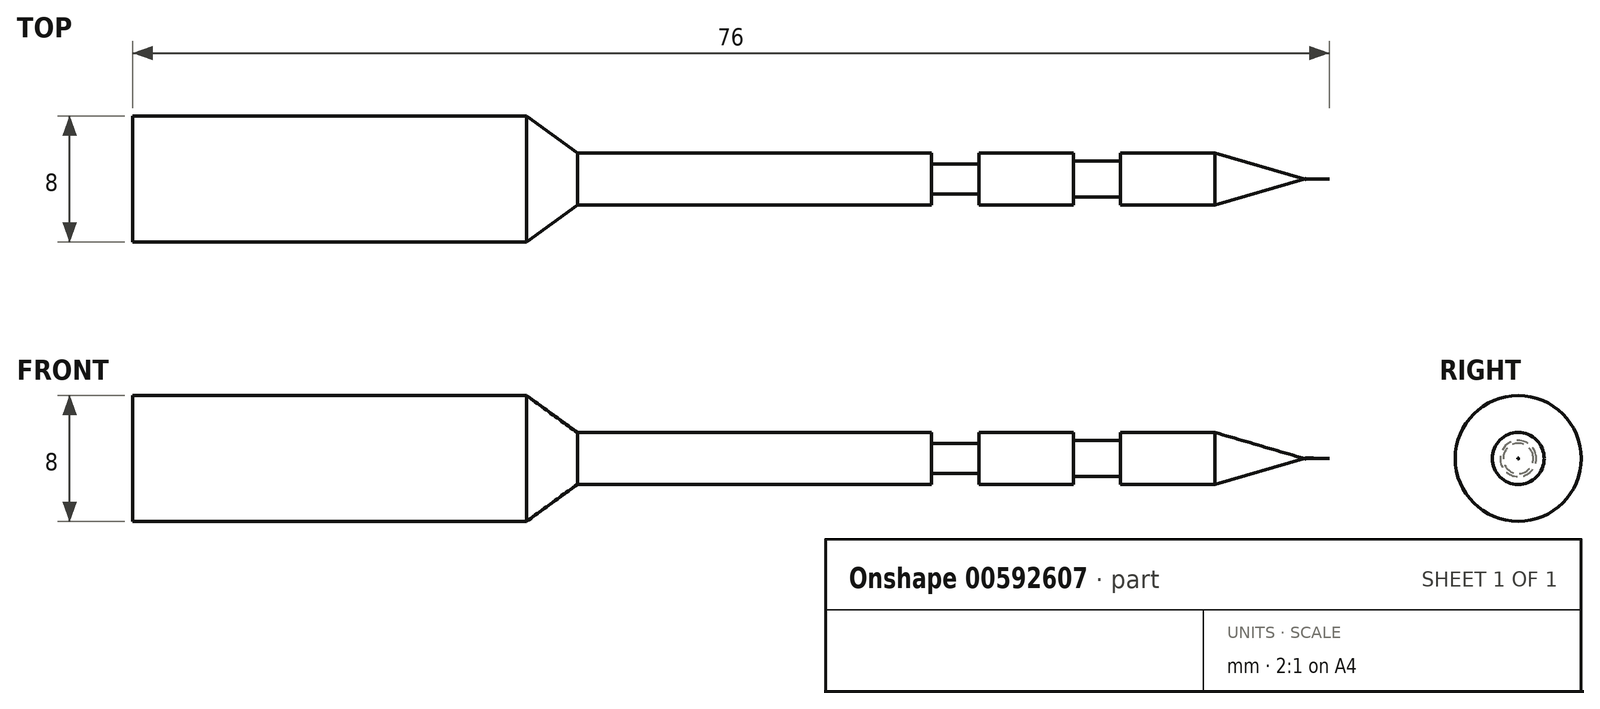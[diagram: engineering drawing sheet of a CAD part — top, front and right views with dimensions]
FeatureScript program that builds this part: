
annotation { "Feature Type Name" : "Feature", "Feature Type Description" : "" }
export const myFeature = defineFeature(function(context is Context, id is Id, definition is map)
    precondition{}
    {
        {
            var Q0;
            Q0=qCreatedBy(makeId("Front.planeOp"),FACE);
            var sketch = newSketch(context, id + "F0", { "sketchPlane" : qUnion([Q0])});
            skLineSegment(sketch, "E0", {"start": v(-71.02, 0) * mm, "end": v(-71.02, 4) * mm});
            skLineSegment(sketch, "E1", {"start": v(-71.02, 4) * mm, "end": v(-46.02, 4) * mm});
            skLineSegment(sketch, "E2", {"start": v(-46.02, 4) * mm, "end": v(-42.78, 1.65) * mm});
            skLineSegment(sketch, "E3", {"start": v(-42.78, 1.65) * mm, "end": v(-20.28, 1.65) * mm});
            skLineSegment(sketch, "E4", {"start": v(-20.28, 1.65) * mm, "end": v(-20.28, 0.96) * mm});
            skLineSegment(sketch, "E5", {"start": v(-20.28, 0.96) * mm, "end": v(-17.28, 0.96) * mm});
            skLineSegment(sketch, "E6", {"start": v(-17.28, 0.96) * mm, "end": v(-17.28, 1.65) * mm});
            skLineSegment(sketch, "E7", {"start": v(-17.28, 1.65) * mm, "end": v(-11.28, 1.65) * mm});
            skLineSegment(sketch, "E8", {"start": v(-11.28, 1.65) * mm, "end": v(-11.28, 1.15) * mm});
            skLineSegment(sketch, "E9", {"start": v(-11.28, 1.15) * mm, "end": v(-8.28, 1.15) * mm});
            skLineSegment(sketch, "E10", {"start": v(-8.28, 1.15) * mm, "end": v(-8.28, 1.65) * mm});
            skLineSegment(sketch, "E11", {"start": v(-8.28, 1.65) * mm, "end": v(-2.28, 1.65) * mm});
            skLineSegment(sketch, "E12", {"start": v(-2.28, 1.65) * mm, "end": v(3.48, -0.03) * mm});
            skLineSegment(sketch, "E13", {"start": v(3.48, -0.03) * mm, "end": v(4.98, 0) * mm});
            skLineSegment(sketch, "E14", {"start": v(4.98, 0) * mm, "end": v(-71.02, 0) * mm});
            skSolve(sketch);
        }
        {
            var Q0;
            Q0 = qSketchRegion(id + "F0", true);
            var Q1;
            Q1=sQuery(id+"F0.wireOp",EDGE,"E14");
            revolve(context, id + "F1", {"entities" : qUnion([Q0]), "axis" : qUnion([Q1]), "revolveType" : RevolveType.FULL});
        }
        {
            var Q0;
            Q0 = qSketchRegion(id + "F0", true);
            var Q1;
            Q1=makeQuery(id+"F1.opRevolve","SWEPT_FACE",FACE,{"disambiguationData":[OSD([sQuery(id+"F0.wireOp",EDGE,"E1")])]});
            revolve(context, id + "F2", {"entities" : qUnion([Q0]), "axis" : qUnion([Q1]), "revolveType" : RevolveType.FULL});
        }
    });
